# Revit family: Domotics-DomesticRanges-GEWISS-CHORUS_COMMAND-ONE-WAY_SWITCH_FAST_WIRING_2M
name_source: partatom
category: Apparecchi elettrici
revit_build: Autodesk Revit 2016 (Build: 20161004_0715(x64)
units: mm (PartAtom-declared; Revit-internal decimal feet)

## family parameters
Condiviso = Sì
Host = Superficie
Mantenere orientamento annotazione = Sì
Numero OmniClass = 23.80.50.11.14
Punto di calcolo locali = Sì
Quota connettore circolare = Usa diametro
Taglio con vuoti quando caricato = Sì
Tipo di parte = Normale
Titolo OmniClass = Switches

## types (15) — shared parameters
Bidimensionale = bidimensionale interruttori 2m : GW12035
Breaking capacity = 1.25 In (200 position changes)
Breaking capacity: = 1.25 In (200 position changes)
Carico apparente = 0 VA
Catalogue = DOMOTICS
Catalogue Range = CHORUS - DOMESTIC RANGE
Category = One-way switch
Electrocod = 0130
Glow Wire Test = 850°C
IDF = 311547f1-3248-405e-b4d8-0f713ec9f59d
IDT = 8b9c9cc9-0f05-4820-9999-e520432aab81
Immagine tipo = GW14035.jpg
Insulation resistance = > 5 MOhm
Larghezza pulsante = 46 mm  [stored 0.150919 ft]
N. poli = 1
No. Chorus modules = 2
Produttore = GEWISS S.p.A.
Prolonged operation (no.of position changes) = 40.000 at In 250 V ac cosÃ˜=0,6
Prospetto di default = 1200 mm
Resistance at test voltage = 2000 V at 50 Hz for 1 minute
SEO = 1 way switch
Simbolo_ = SIMBOLO INTERRUTTORI : INT2PLUM
Standard = EN 60669-1
Standard; = EN 60669-1
Technical sheet = https://www.gewiss.com
Terminal grip on cable traction = > 50 N
Terminal tightening capacity = min. 0,75 - max. 2x4
Terminal tightening capacity flexible cables (mm2) = min. 0,75 - max. 2x4
Terminal tightening capacity rigid cables (mm2) = min. 0,5 - max. 2x2,5
Thermo-pressure with ball = 125
Tipo_ = CHORUS INTERRUTTORI 2M_BASE : GW14035 - Titanio - Illuminabile segnalazione
URL = https://www.gewiss.com
Version file RFA = 19.0
Volt = 230 V
Voltage = 250 V ac
Voltage: = 250 V ac
Wiring terminals = Quick, with spring
pulsante = GEWISS TITANIO
pulsante nero = GEWISS ACCIAIO NERO

## per-type parameters (varying)
| type | Button key | Colour | Description: | Descrizione | EAN code | Modello | Type |
| GW10034F - 1-way switch 2M 2P 16AX fast wiring White | Neutral | White | 2P - 16 AX | 1-WAY SWITCH, 2M 2P 16AX R.WIRING WHITE | 8011564258792 | GW10034F | General |
| GW10033F - 1-way switch 2M 1P 16AX illuminable fast wiring White | With replaceable neutral lens | White | 1P - 16AX illuminable | 1-WAY SWITCH, 2M 1P 16AX ILL SIG R.W. W | 8011564258778 | GW10033F | Indicator |
| GW12032F - 1-way switch 2M 1P 16AX illuminable fast wiring Black | With diffuser | Black | 1P - 16AX illuminable | 1-WAY SWITCH, 2M 1P 16AX ILL LOC R.W. B | 8011564269828 | GW12032F | Backlit |
| GW10032F - 1-way switch 2M 1P 16AX illuminable fast wiring White | With diffuser | White | 1P - 16AX illuminable | 1-WAY SWITCH, 2M 1P 16AX ILL LOC R.W. W | 8011564258754 | GW10032F | Backlit |
| GW14034F - 1-way switch 2M 2P 16AX fast wiring Titanium | Neutral | Titanium | 2P - 16 AX | 1-WAY SWITCH 2M 2P 16AX R.W. TITANIUM | 8011564265479 | GW14034F | General |
| GW14031F - 1-way switch 2M 1P 16AX fast wiring Titanium | Neutral | Titanium | 1P - 16AX | 1-WAY SWITCH 2M 1P 16AX R.W. TITANIUM | 8011564265417 | GW14031F | General |
| GW10031F - 1-way switch 2M 1P 16AX fast wiring White | Neutral | White | 1P - 16AX | 1-WAY SWITCH, 2M 1P 16AX R.WIRING WHITE | 8011564258730 | GW10031F | General |
| GW10035F - 1-way switch 2M 2P 16AX illuminable fast wiring White | With replaceable neutral lens | White | 2P - 16AX illuminable | 1-WAY SWITCH, 2M 2P 16AX ILL SIG R.W. W | 8011564258815 | GW10035F | Indicator |
| GW12031F - 1-way switch 2M 1P 16AX fast wiring Black | Neutral | Black | 1P - 16AX | 1-WAY SWITCH, 2M 1P 16AX R.WIRING BLACK | 8011564269811 | GW12031F | General |
| GW14033F - 1-way switch 2M 1P 16AX illuminable fast wiring Titanium | With replaceable neutral lens | Titanium | 1P - 16AX illuminable | 1-WAY SWITCH 2M 1P 16AX ILL SIG R.W. T | 8011564265455 | GW14033F | Indicator |
| GW12035F - 1-way switch 2M 2P 16AX illuminable fast wiring Black | With replaceable neutral lens | Black | 2P - 16AX illuminable | 1-WAY SWITCH, 2M 2P 16AX ILL SIG R.W. B | 8011564269859 | GW12035F | Indicator |
| GW12033F - 1-way switch 2M 1P 16AX illuminable fast wiring Black | With replaceable neutral lens | Black | 1P - 16AX illuminable | 1-WAY SWITCH, 2M 1P 16AX ILL SIG R.W. B | 8011564269835 | GW12033F | Indicator |
| GW12034F - 1-way switch 2M 2P 16AX fast wiring Black | Neutral | Black | 2P - 16 AX | 1-WAY SWITCH, 2M 2P 16AX R.WIRING BLACK | 8011564269842 | GW12034F | General |
| GW14035F - 1-way switch 2M 2P 16AX illuminable fast wiring Titanium | With replaceable neutral lens | Titanium | 2P - 16AX illuminable | 1-WAY SWITCH 2M 2P 16AX ILL SIG R.W. T | 8011564265493 | GW14035F | Indicator |
| GW14032F - 1-way switch 2M 1P 16AX illuminable fast wiring Titanium | With diffuser | Titanium | 1P - 16AX illuminable | 1-WAY SWITCH 2M 1P 16AX ILL LOC R.W. T | 8011564265431 | GW14032F | Backlit |

note: source unit labels omitted for Thermo-pressure with ball — the stored unit's dimension contradicts the parameter name (converter mislabeling)

note: [stored X ft] marks values corroborated as IEEE doubles in the binary element streams (Revit-internal decimal feet)
